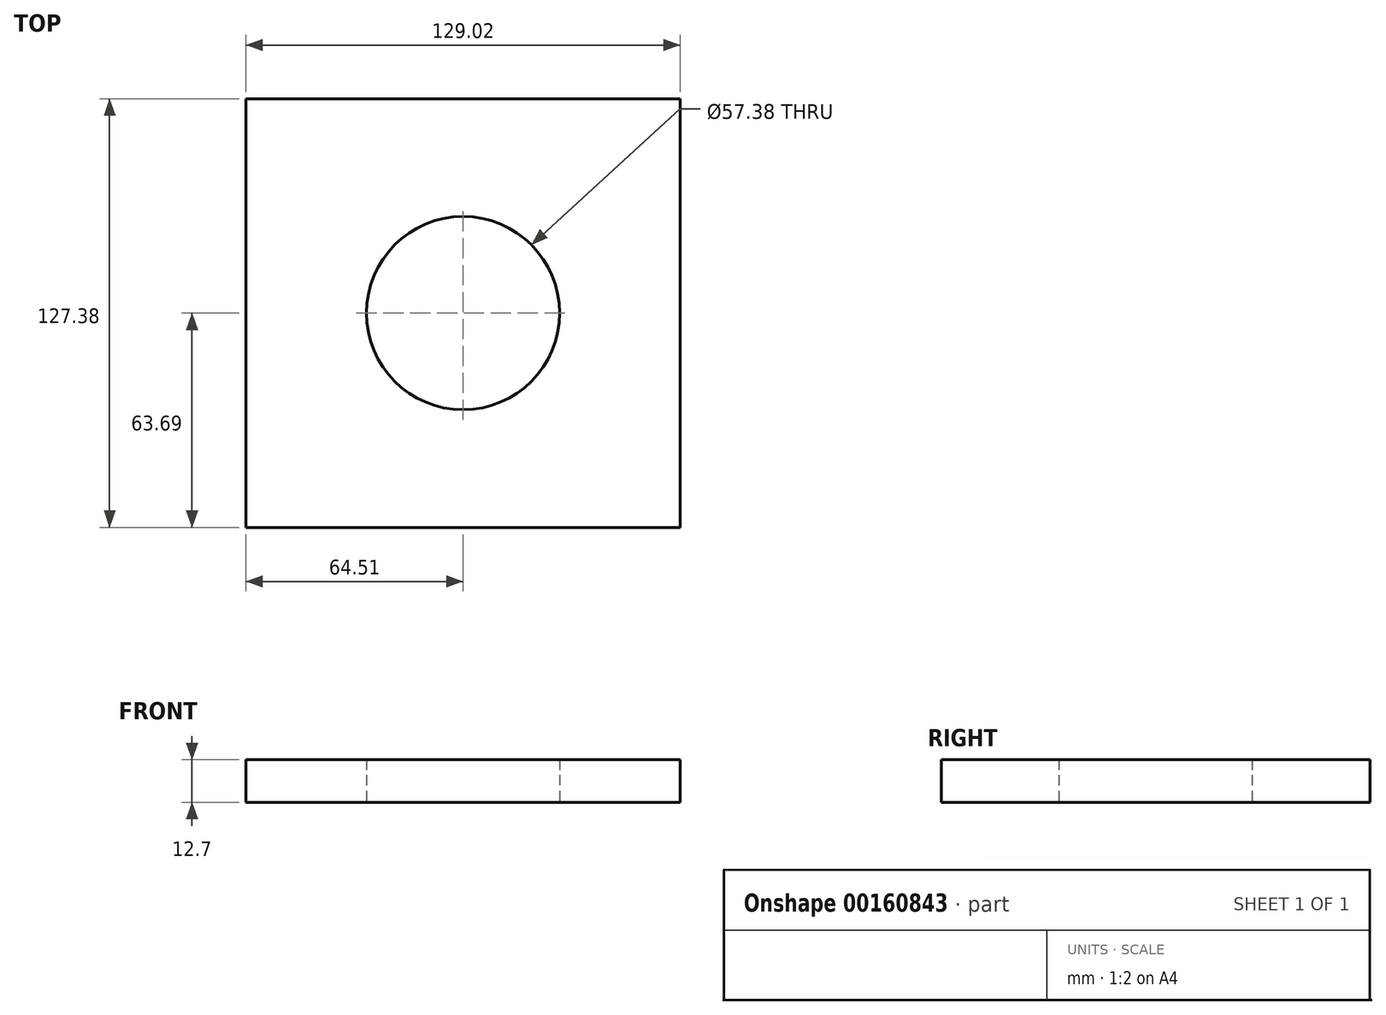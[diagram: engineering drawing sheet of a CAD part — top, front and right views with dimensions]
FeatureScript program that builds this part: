
annotation { "Feature Type Name" : "Feature", "Feature Type Description" : "" }
export const myFeature = defineFeature(function(context is Context, id is Id, definition is map)
    precondition{}
    {
        {
            var Q0;
            Q0=qCreatedBy(makeId("Top.planeOp"),FACE);
            var sketch = newSketch(context, id + "F0", { "sketchPlane" : qUnion([Q0])});
            skLineSegment(sketch, "E0.bottom", {"start": v(64.5, -63.7) * mm, "end": v(-64.5, -63.7) * mm});
            skLineSegment(sketch, "E0.top", {"start": v(64.5, 63.7) * mm, "end": v(-64.5, 63.7) * mm});
            skLineSegment(sketch, "E0.left", {"start": v(64.5, -63.7) * mm, "end": v(64.5, 63.7) * mm});
            skLineSegment(sketch, "E0.right", {"start": v(-64.5, -63.7) * mm, "end": v(-64.5, 63.7) * mm});
            skPoint(sketch, "E0.middle", {"position": v(0, 0) * mm});
            skCircle(sketch, "E1", {"center": v(0, 0) * mm, "radius": 28.7 * mm});
            skSolve(sketch);
        }
        {
            var Q0;
            Q0=makeQuery(id+"F0.imprint","IMPRINT",FACE,{"disambiguationData":[TD([[makeQuery(id+"F0.imprint","IMPRINT",EDGE,{"derivedFrom":sQuery(id+"F0.wireOp",EDGE,"E0.bottom")}),-1.0]])]});
            extrude(context, id + "F1", {"entities" : qUnion([Q0]), "depth" : 12.7 * mm});
        }
    });
